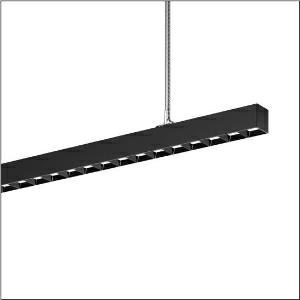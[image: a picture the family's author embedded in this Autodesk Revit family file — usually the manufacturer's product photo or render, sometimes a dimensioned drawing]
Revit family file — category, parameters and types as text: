
# Revit family: silica_r__21_51mx31dc3dbb_16a7
name_source: partatom
category: Lighting Fixtures
units: mm (PartAtom-declared; Revit-internal decimal feet)

## family parameters
Cut with Voids When Loaded = No
Host = Face
Light Source = No
Part Type = Normal
Room Calculation Point = No
Round Connector Dimension = Use Diameter
Shared = No

## types (1)
- --- (1 x LED, 18230 lm, 113.3 W, 3000K)
    Apparent Load = 113 VA
    CIE Flux Codes = 87 99 100 59 100
    Color Rendering = 80
    Color Temperature = 3000K
    Default Elevation = 1800 mm
    Description = Silica® 21, office luminaire, primary light control with darklight reflector, of PMMA, black, CAT 2 (L<= 3000cd/m²), light emission: direct/indirect distribution, primary light characteristic: symmetric, installation type: suspended mounting, LED, rated luminous flux: 18.230lm, luminous efficacy: 161lm/W, light colour: 830, colour temperature: 3000K, with terminal, 3+2-pole, max. 2.5mm², mains connection: 220..240V, AC, 50/60Hz, rated input power: 113.3W, luminaire housing, of aluminium, jet black (RAL 9005), length: 3.004mm, width: 53mm, height: 53mm, protection rating (complete): IP20, insulation class (complete): insulation class I (protective earthing), certification: CE, permissible operating ambient temperature: 0..+35°C, standard: EN 50419, packaging unit: 1 piece
    Height = 53 mm
    Lamp = 1 x LED
    Lamp Light Flux = 18230 lm
    Lamp Power = 113.3 W
    Lamp count = 1
    Length = 3004 mm
    Luminous efficacy = 161 lm/W
    Manufacturer = Siteco
    ModVariant = No
    Model = 51MX31DC3DBB
    Mounting Place = Ceiling
    Mounting Type = Pendant
    Number of Poles = 1
    OnlyDefault = Yes
    Power Factor = 1
    Product Name = Silica® 21
    Product group = office luminaire | ceiling pendant
    ProductGroupID = 902
    Protection Class = Protection class I
    Protection Degree = IP 20
    RLX_Detail_Level = 1
    RLX_Emergency_Light_Flux = 0 lm
    RLX_Emergency_Type = 0
    RLX_Emergency_Type_DB = No
    RlxData = <blob elided: 67165 chars, md5=42778159>
    Socket = socket
    Standby Power = 0 W
    System Light Flux = 18230 lm
    System Power = 113 W
    Type Comments = factory setting: luminous flux: 100 % | dim-lin: 254 | 392 mA
    Type Image = l_1313617.jpg
    URL = http://relux.com
    VarID = @adj_069913
    Voltage = 0 V
    Weight = 0.00 kg
    Width = 53 mm

## geometry (parser evidence)
native form markers: Blend x4, Sweep x14
no freeform markers — native parametric forms only
